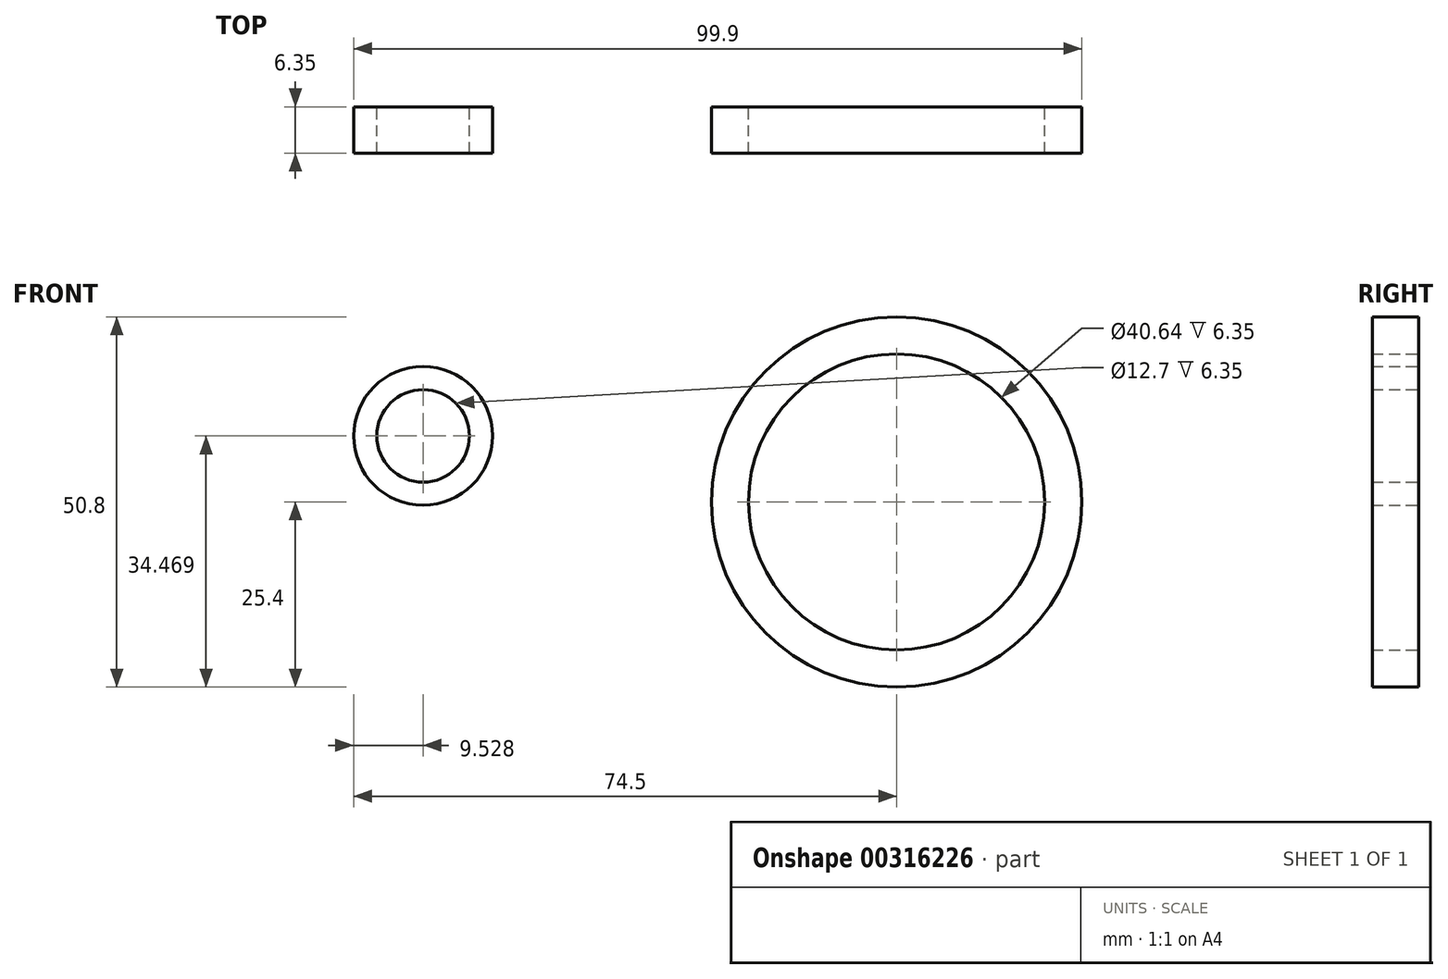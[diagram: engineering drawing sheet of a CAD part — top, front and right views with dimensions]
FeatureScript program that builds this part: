
annotation { "Feature Type Name" : "Feature", "Feature Type Description" : "" }
export const myFeature = defineFeature(function(context is Context, id is Id, definition is map)
    precondition{}
    {
        {
            var Q0;
            Q0=qCreatedBy(makeId("Front.planeOp"),FACE);
            var sketch = newSketch(context, id + "F0", { "sketchPlane" : qUnion([Q0])});
            skCircle(sketch, "E0", {"center": v(0, 0) * mm, "radius": 20.32 * mm});
            skCircle(sketch, "E1", {"center": v(0, 0) * mm, "radius": 25.4 * mm});
            skSolve(sketch);
        }
        {
            var Q0;
            Q0=qCreatedBy(makeId("Front.planeOp"),FACE);
            var sketch = newSketch(context, id + "F1", { "sketchPlane" : qUnion([Q0])});
            skCircle(sketch, "E2", {"center": v(-64.97, 9.07) * mm, "radius": 6.35 * mm});
            skCircle(sketch, "E3", {"center": v(-64.97, 9.07) * mm, "radius": 9.53 * mm});
            skSolve(sketch);
        }
        {
            var Q0;
            Q0=makeQuery(id+"F0.imprint","IMPRINT",FACE,{"disambiguationData":[TD([[makeQuery(id+"F0.imprint","IMPRINT",EDGE,{"derivedFrom":sQuery(id+"F0.wireOp",EDGE,"E0")}),-1.0]])]});
            extrude(context, id + "F2", {"entities" : qUnion([Q0]), "depth" : 6.35 * mm});
        }
        {
            var Q0;
            Q0=makeQuery(id+"F1.imprint","IMPRINT",FACE,{"disambiguationData":[TD([[makeQuery(id+"F1.imprint","IMPRINT",EDGE,{"derivedFrom":sQuery(id+"F1.wireOp",EDGE,"E2")}),-1.0]])]});
            extrude(context, id + "F3", {"entities" : qUnion([Q0]), "depth" : 6.35 * mm});
        }
    });
